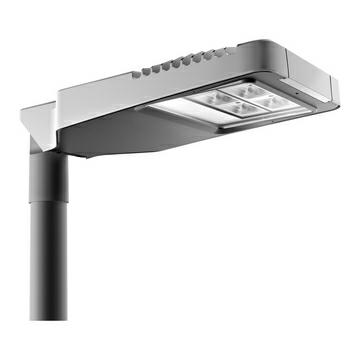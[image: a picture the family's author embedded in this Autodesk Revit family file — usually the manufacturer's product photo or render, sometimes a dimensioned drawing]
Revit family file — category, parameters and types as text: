
# Revit family: Lighting-Stradale-GEWISS-ROAD[5]MEDIUM-LED_OTTICA_WIDE_CLI
name_source: partatom
category: Apparecchi per illuminazione
units: mm (PartAtom-declared; Revit-internal decimal feet)

## family parameters
Basato su piano di lavoro = No
Condiviso = No
Punto di calcolo locali = No
Quota connettore circolare = Usa diametro
Sempre verticale = Sì
Sorgente d'illuminazione = No
Taglio con vuoti quando caricato = No
Tipo di parte = Normale

## types (1)
- Lighting-Stradale-GEWISS-ROAD[5]MEDIUM-LED_OTTICA_WIDE_CLI
    Alimentatore = Incluso
    Apparecchio a ridotta temperatura superficiale = -
    Applicazione = Esterno
    Cablaggio = Sezionatore
    Caratteristiche elettriche e gestione della luce = -
    Caratteristiche ottiche e illuminotecniche = -
    Catalogo = LIGHTING
    Catalogo Serie = ROAD [5]
    Certificazione DIN 18032-3 = -
    Certificazioni e classificazioni = -
    Classe fotobiologica = RG0
    Classe isolamento = I
    Classificazione: = -
    Codice Electrocod = 244C
    Codice digitale univoco (Datamatrix) = Attualmente non presente
    Colore = Grigio grafite
    Contesto = Illuminazione stradale e parcheggi
    Controllo abbagliamento e luminanza = G*3 - ULOR = 0
    Corpo = Alluminio pressofuso
    Corrente di pilotaggio. = 0,7A
    Descrizione = GWR5776M30K - ROAD5 MEDI WIDE 6M 3000K 0,7A CL1 1-10V
    Dispositivo di protezione = DM 10KV / CM 10KV
    Distanza minima dall'oggetto illuminato = 1M
    Durata di vita = L90B10 (Tq+25°C) = 100.000 h - L90B10 (Tq+50°C) = 50.000 h
    Efficienza luminosa (lm/W) = 102
    Finitura colore = Verniciato a polveri
    Fissaggio = Testa palo - Sbraccio
    Flusso nominale (lm) = 16200
    Frequenza nominale (Hz) = 50 / 60
    Funzionalità alimentatore = Dimmerabile
    Gancio di chiusura = Maniglia frontale integrata
    Garanzia = 5 anni
    Grado di protezione = IP66
    Gruppo ottico = Riflettore in PC metallizzato
    Guarnizioni = silicone antinvecchiamento
    IDF = ec2352d5-93a7-44e2-a8fa-3a508d6b870d
    IDT = c439c4f296dc4bdaaede42b4d003d5bb
    IPEA = STRADALE = A // GRANDI AREE = A3+ // CICLOPEDONALI = A // AREE VERDI = A // CENTRO STORICO = A4+
    Immagine tipo = GWR5276M.jpg
    Inclinazione = -20° ÷ +10° sbraccio - -10° ÷ +20° testa palo
    Indice di resa cromatica = CRI-70
    Informazioni generali = -
    Installazione e manutenzione = -
    LED Life Time (L80B05) = 77000H
    Lampada = LED
    Lampada: = LED
    Lumen output (lm) = 16500
    Materiali = -
    Modello = GWR5776M30K
    Norma di riferimento = EN 60598-2-3, EN 60598-1 IEC/TR 62778
    Numero moduli = 6 (6x3 LED)
    Ottica = WIDE
    Peso (kg): = 9,09999999999999
    Potenza assorbita : = 161 W @ 0.7A
    Potenza di sistema = 159W
    Produttore = GEWISS S.p.A.
    Regolazione inclinazione = -20° ÷ +10° sbraccio - -10° ÷ +20° testa palo
    Resistenza agli urti = IK08
    Resistenza al filo incandescente = -
    Resistenza alle sovratensioni : = 10 KV in modalità comune e differenziale
    SEO = Stradale
    Scheda Tecnica = https://www.gewiss.com
    Schermo = Vetro piano temperato spessore 4mm
    Sistema di controllo = Dimmerabile 1-10 V
    Sostituibilità gruppo ottico = Non disponibile
    Sostituibilità piastra di cablaggio = Non disponibile
    Superficie massima esposta al vento = 0,19M2
    Superficie massima esposta al vento : = 0.19 m2
    Temperatura di colore = 3000K
    Temperatura di colore: = 3000 K (CRI>80)
    Temperatura di esercizio = -25 +50 °C
    Temperatura di stoccaggio = -
    Temperatura di utilizzo = -25 +50 °C
    Tensione = 220/240 V - 50/60 Hz - Dimmerabile 1-10 V
    Tensione di alimentazione = 220 - 240 V
    Tipo alimentatore = Driver Led in corrente continua
    Tipo di apparecchio = Apparecchiatura stradale a LED
    Tipo di installazione e montaggio = Testa palo - Sbraccio
    Tipologia = Dimmerabile
    Tipologia sorgente luminosa = LED - Non sostituibile
    Tolleranza cromatica = SDCM = 5
    URL = https://www.gewiss.com
    Vano di alimentazione = Integrato
    Versione file RFA = 20.11
    Viti esterne = Acciaio inox

## geometry (parser evidence)
native form markers: Blend x2
no freeform markers — native parametric forms only
